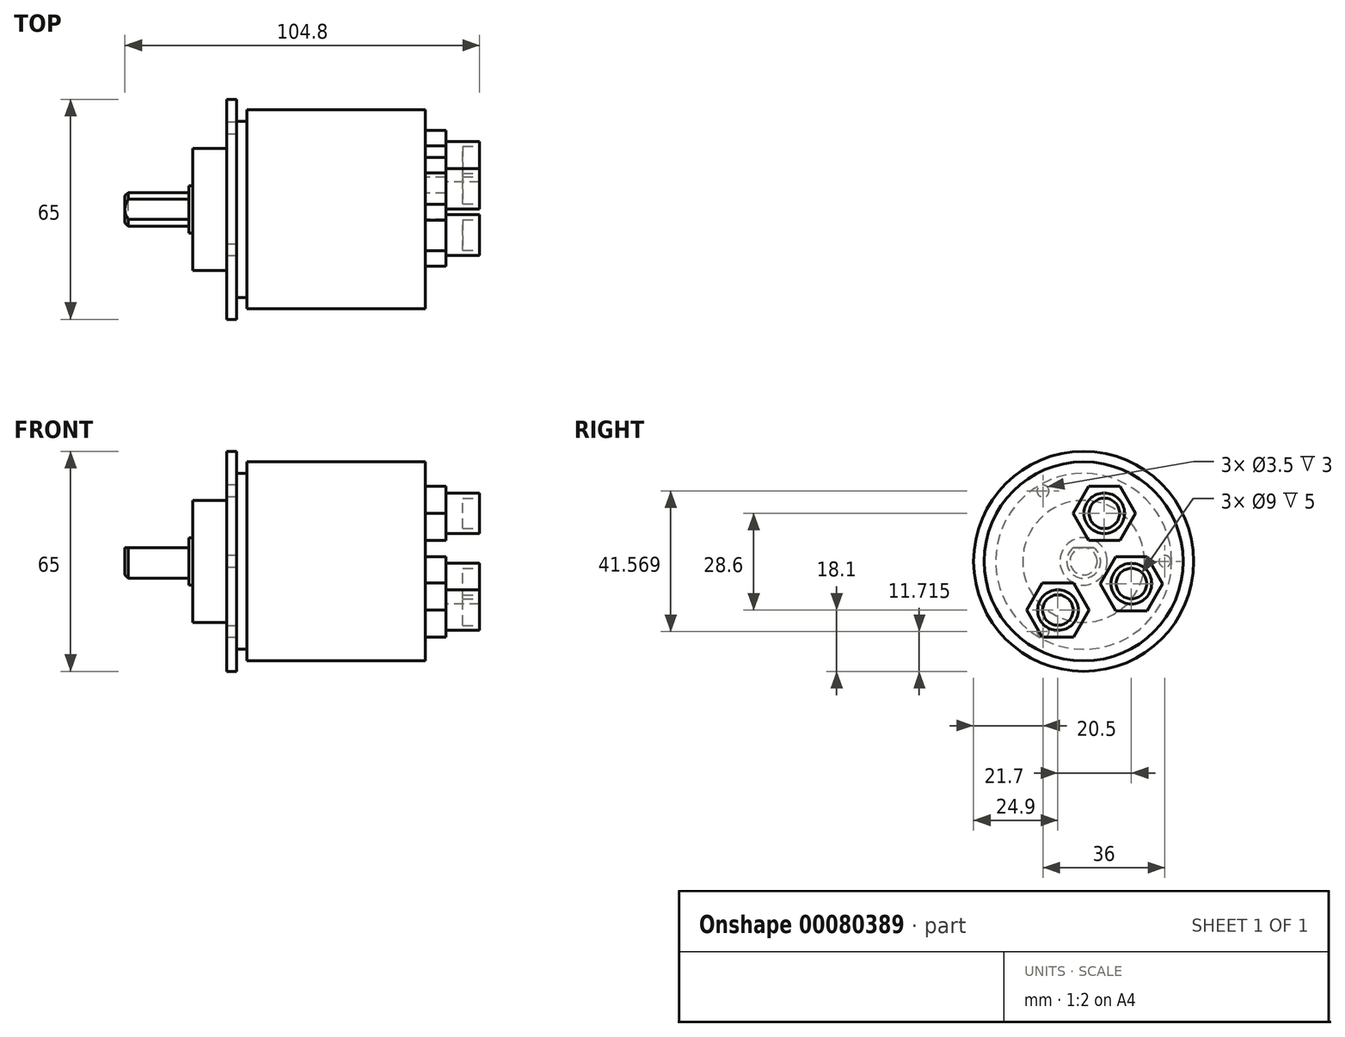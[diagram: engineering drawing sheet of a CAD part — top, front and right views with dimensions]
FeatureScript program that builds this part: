
annotation { "Feature Type Name" : "Feature", "Feature Type Description" : "" }
export const myFeature = defineFeature(function(context is Context, id is Id, definition is map)
    precondition{}
    {
        {
            var Q0;
            Q0=qCreatedBy(makeId("Right.planeOp"),FACE);
            var sketch = newSketch(context, id + "F0", { "sketchPlane" : qUnion([Q0])});
            skCircle(sketch, "E0", {"center": v(0, 0) * mm, "radius": 5 * mm});
            skSolve(sketch);
        }
        {
            var Q0;
            Q0=qSketchRegion(id+"F0",true);
            extrude(context, id + "F1", {"entities" : qUnion([Q0]), "oppositeDirection" : true, "depth" : 18.9 * mm});
        }
        {
            var Q0;
            Q0=qCreatedBy(makeId("Right.planeOp"),FACE);
            var sketch = newSketch(context, id + "F2", { "sketchPlane" : qUnion([Q0])});
            skLineSegment(sketch, "E1", {"start": v(-18, 0) * mm, "end": v(18.18, 0) * mm, "construction": true});
            skLineSegment(sketch, "E2.0", {"start": v(-18, 4) * mm, "end": v(18.18, 4) * mm});
            skLineSegment(sketch, "E3.bottom", {"start": v(-10.5, 4) * mm, "end": v(10.66, 4) * mm});
            skLineSegment(sketch, "E3.top", {"start": v(-10.5, 8.93) * mm, "end": v(10.66, 8.93) * mm});
            skLineSegment(sketch, "E3.left", {"start": v(-10.5, 4) * mm, "end": v(-10.5, 8.93) * mm});
            skLineSegment(sketch, "E3.right", {"start": v(10.66, 4) * mm, "end": v(10.66, 8.93) * mm});
            skLineSegment(sketch, "E4.0", {"start": v(-18, -5) * mm, "end": v(18.18, -5) * mm, "construction": true});
            skSolve(sketch);
        }
        {
            var Q0;
            Q0=qSketchRegion(id+"F2",true);
            extrude(context, id + "F3", {"entities" : qUnion([Q0]), "operationType" : NewBodyOperationType.REMOVE, "endBound" : BoundingType.THROUGH_ALL, "oppositeDirection" : true, "depth" : 25 * mm});
        }
        {
            var Q0;
            Q0=makeQuery(id+"F1.opExtrude","CAP_EDGE",EDGE,{"disambiguationData":[OSD([sQuery(id+"F0.wireOp",EDGE,"E0")])],"isStart":false});
            chamfer(context, id + "F4", {"entities" : qUnion([Q0]), "width" : 1 * mm, "tangentPropagation" : true});
        }
        {
            var Q0;
            Q0=makeQuery(id+"F1.opExtrude","CAP_FACE",FACE,{"disambiguationData":[OSD([sQuery(id+"F0.wireOp",EDGE,"E0")])],"isStart":true});
            var sketch = newSketch(context, id + "F5", { "sketchPlane" : qUnion([Q0])});
            skCircle(sketch, "E5", {"center": v(0, 0) * mm, "radius": 7 * mm});
            skSolve(sketch);
        }
        {
            var Q0;
            Q0=qSketchRegion(id+"F5",true);
            extrude(context, id + "F6", {"entities" : qUnion([Q0]), "operationType" : NewBodyOperationType.ADD, "depth" : 1.1 * mm});
        }
        {
            var Q0;
            Q0=makeQuery(id+"F6.opExtrude","CAP_FACE",FACE,{"disambiguationData":[OSD([sQuery(id+"F5.wireOp",EDGE,"E5")])],"isStart":false});
            var sketch = newSketch(context, id + "F7", { "sketchPlane" : qUnion([Q0])});
            skCircle(sketch, "E6", {"center": v(0, 0) * mm, "radius": 18 * mm});
            skSolve(sketch);
        }
        {
            var Q0;
            Q0=qSketchRegion(id+"F7",true);
            extrude(context, id + "F8", {"entities" : qUnion([Q0]), "operationType" : NewBodyOperationType.ADD, "depth" : 10 * mm});
        }
        {
            var Q0;
            Q0=makeQuery(id+"F8.opExtrude","CAP_FACE",FACE,{"disambiguationData":[OSD([sQuery(id+"F7.wireOp",EDGE,"E6")])],"isStart":false});
            var sketch = newSketch(context, id + "F9", { "sketchPlane" : qUnion([Q0])});
            skCircle(sketch, "E7", {"center": v(0, 0) * mm, "radius": 32.5 * mm});
            skSolve(sketch);
        }
        {
            var Q0;
            Q0=qSketchRegion(id+"F9",true);
            extrude(context, id + "F10", {"entities" : qUnion([Q0]), "operationType" : NewBodyOperationType.ADD, "depth" : 3 * mm});
        }
        {
            var Q0;
            Q0=makeQuery(id+"F10.opExtrude","CAP_FACE",FACE,{"disambiguationData":[OSD([sQuery(id+"F9.wireOp",EDGE,"E7")])],"isStart":false});
            var sketch = newSketch(context, id + "F11", { "sketchPlane" : qUnion([Q0])});
            skCircle(sketch, "E8", {"center": v(0, 0) * mm, "radius": 26 * mm});
            skSolve(sketch);
        }
        {
            var Q0;
            Q0=qSketchRegion(id+"F11",true);
            extrude(context, id + "F12", {"entities" : qUnion([Q0]), "operationType" : NewBodyOperationType.ADD, "depth" : 3 * mm});
        }
        {
            var Q0;
            Q0=makeQuery(id+"F10.opExtrude","CAP_FACE",FACE,{"disambiguationData":[OSD([sQuery(id+"F9.wireOp",EDGE,"E7")])],"isStart":true});
            cPlane(context, id + "F13", {"entities" : qUnion([Q0]), "cplaneType" : CPlaneType.OFFSET, "offset" : 58.8 * mm, "oppositeDirection" : true, "width" : 150 * mm, "height" : 150 * mm});
        }
        {
            var Q0;
            Q0=qCreatedBy(id+"F13.planeOp",FACE);
            var sketch = newSketch(context, id + "F14", { "sketchPlane" : qUnion([Q0])});
            skCircle(sketch, "E9", {"center": v(0, 0) * mm, "radius": 29.4 * mm});
            skSolve(sketch);
        }
        {
            var Q0;
            Q0=qSketchRegion(id+"F14",true);
            var Q1;
            Q1=makeQuery(id+"F12.opExtrude","CAP_FACE",FACE,{"disambiguationData":[OSD([sQuery(id+"F11.wireOp",EDGE,"E8")])],"isStart":false});
            extrude(context, id + "F15", {"entities" : qUnion([Q0]), "operationType" : NewBodyOperationType.ADD, "endBound" : BoundingType.UP_TO_SURFACE, "endBoundEntityFace" : qUnion([Q1]), "depth" : 25 * mm});
        }
        {
            var Q0;
            Q0=makeQuery(id+"F10.opExtrude","CAP_FACE",FACE,{"disambiguationData":[OSD([sQuery(id+"F9.wireOp",EDGE,"E7")])],"isStart":true});
            var sketch = newSketch(context, id + "F16", { "sketchPlane" : qUnion([Q0])});
            skLineSegment(sketch, "E10", {"start": v(0, 0) * mm, "end": v(-37.53, 0) * mm, "construction": true});
            skCircle(sketch, "E11", {"center": v(0, 0) * mm, "radius": 24 * mm, "construction": true});
            skPoint(sketch, "E12", {"position": v(-24, 0) * mm});
            skPoint(sketch, "E13.1.0", {"position": v(12, -20.78) * mm});
            skPoint(sketch, "E13.2.0", {"position": v(12, 20.78) * mm});
            skCircle(sketch, "E14", {"center": v(-24, 0) * mm, "radius": 1.75 * mm});
            skCircle(sketch, "E15.1.0", {"center": v(12, -20.78) * mm, "radius": 1.75 * mm});
            skCircle(sketch, "E15.2.0", {"center": v(12, 20.78) * mm, "radius": 1.75 * mm});
            skSolve(sketch);
        }
        {
            var Q0;
            Q0=qSketchRegion(id+"F16",true);
            extrude(context, id + "F17", {"entities" : qUnion([Q0]), "operationType" : NewBodyOperationType.REMOVE, "oppositeDirection" : true, "depth" : 3 * mm});
        }
        {
            var Q0;
            Q0=makeQuery(id+"F15.opExtrude","CAP_FACE",FACE,{"disambiguationData":[OSD([sQuery(id+"F14.wireOp",EDGE,"E9")])],"isStart":true});
            var sketch = newSketch(context, id + "F18", { "sketchPlane" : qUnion([Q0])});
            skLineSegment(sketch, "E16", {"start": v(0, 47.06) * mm, "end": v(0, -42.51) * mm, "construction": true});
            skLineSegment(sketch, "E17", {"start": v(0, 0) * mm, "end": v(46.06, 0) * mm, "construction": true});
            skLineSegment(sketch, "E18", {"start": v(0, 0) * mm, "end": v(42.94, -20.02) * mm, "construction": true});
            skLineSegment(sketch, "E19.0", {"start": v(14.1, 45.36) * mm, "end": v(14.1, -42.51) * mm, "construction": true});
            skLineSegment(sketch, "E20", {"start": v(0, 0) * mm, "end": v(-39.96, 0) * mm, "construction": true});
            skLineSegment(sketch, "E21.0", {"start": v(6.1, 14.2) * mm, "end": v(-39.96, 14.2) * mm, "construction": true});
            skLineSegment(sketch, "E22.0", {"start": v(6.1, 47.06) * mm, "end": v(6.1, -42.51) * mm, "construction": true});
            skPoint(sketch, "E23", {"position": v(6.1, 14.2) * mm});
            skPoint(sketch, "E24", {"position": v(14.1, -6.57) * mm});
            skLineSegment(sketch, "E25.0", {"start": v(0, -14.4) * mm, "end": v(-39.96, -14.4) * mm, "construction": true});
            skLineSegment(sketch, "E26.0", {"start": v(-7.6, 47.06) * mm, "end": v(-7.6, -42.51) * mm, "construction": true});
            skPoint(sketch, "E27", {"position": v(-7.6, -14.4) * mm});
            skCircle(sketch, "E28.cCircle", {"center": v(14.1, -6.57) * mm, "radius": 8 * mm});
            skLineSegment(sketch, "E28.0", {"start": v(9.48, 1.43) * mm, "end": v(18.72, 1.43) * mm});
            skLineSegment(sketch, "E28.1", {"start": v(18.72, 1.43) * mm, "end": v(23.34, -6.57) * mm});
            skLineSegment(sketch, "E28.2", {"start": v(23.34, -6.57) * mm, "end": v(18.72, -14.57) * mm});
            skLineSegment(sketch, "E28.3", {"start": v(18.72, -14.57) * mm, "end": v(9.48, -14.57) * mm});
            skLineSegment(sketch, "E28.4", {"start": v(9.48, -14.57) * mm, "end": v(4.86, -6.57) * mm});
            skLineSegment(sketch, "E28.5", {"start": v(4.86, -6.57) * mm, "end": v(9.48, 1.43) * mm});
            skPoint(sketch, "E28.0.midPoint", {"position": v(14.1, 1.43) * mm});
            skCircle(sketch, "E29.cCircle", {"center": v(6.1, 14.2) * mm, "radius": 8 * mm, "construction": true});
            skLineSegment(sketch, "E29.0", {"start": v(1.48, 22.2) * mm, "end": v(10.72, 22.2) * mm});
            skLineSegment(sketch, "E29.1", {"start": v(10.72, 22.2) * mm, "end": v(15.34, 14.2) * mm});
            skLineSegment(sketch, "E29.2", {"start": v(15.34, 14.2) * mm, "end": v(10.72, 6.2) * mm});
            skLineSegment(sketch, "E29.3", {"start": v(10.72, 6.2) * mm, "end": v(1.48, 6.2) * mm});
            skLineSegment(sketch, "E29.4", {"start": v(1.48, 6.2) * mm, "end": v(-3.14, 14.2) * mm});
            skLineSegment(sketch, "E29.5", {"start": v(-3.14, 14.2) * mm, "end": v(1.48, 22.2) * mm});
            skPoint(sketch, "E29.0.midPoint", {"position": v(6.1, 22.2) * mm});
            skCircle(sketch, "E30.cCircle", {"center": v(-7.6, -14.4) * mm, "radius": 8 * mm, "construction": true});
            skLineSegment(sketch, "E30.0", {"start": v(-12.22, -6.4) * mm, "end": v(-2.98, -6.4) * mm});
            skLineSegment(sketch, "E30.1", {"start": v(-2.98, -6.4) * mm, "end": v(1.64, -14.4) * mm});
            skLineSegment(sketch, "E30.2", {"start": v(1.64, -14.4) * mm, "end": v(-2.98, -22.4) * mm});
            skLineSegment(sketch, "E30.3", {"start": v(-2.98, -22.4) * mm, "end": v(-12.22, -22.4) * mm});
            skLineSegment(sketch, "E30.4", {"start": v(-12.22, -22.4) * mm, "end": v(-16.84, -14.4) * mm});
            skLineSegment(sketch, "E30.5", {"start": v(-16.84, -14.4) * mm, "end": v(-12.22, -6.4) * mm});
            skPoint(sketch, "E30.0.midPoint", {"position": v(-7.6, -6.4) * mm});
            skSolve(sketch);
        }
        {
            var Q0;
            Q0=qSketchRegion(id+"F18",true);
            extrude(context, id + "F19", {"entities" : qUnion([Q0]), "operationType" : NewBodyOperationType.ADD, "depth" : 6 * mm});
        }
        {
            var Q0;
            Q0=makeQuery(id+"F19.opExtrude","CAP_FACE",FACE,{"disambiguationData":[OSD([sQuery(id+"F18.wireOp",EDGE,"E29.0"),sQuery(id+"F18.wireOp",EDGE,"E29.1"),sQuery(id+"F18.wireOp",EDGE,"E29.2"),sQuery(id+"F18.wireOp",EDGE,"E29.3"),sQuery(id+"F18.wireOp",EDGE,"E29.4"),sQuery(id+"F18.wireOp",EDGE,"E29.5")])],"isStart":false});
            var sketch = newSketch(context, id + "F20", { "sketchPlane" : qUnion([Q0])});
            skPoint(sketch, "E31.0", {"position": v(6.1, 14.2) * mm});
            skPoint(sketch, "E32.0", {"position": v(14.1, -6.57) * mm});
            skPoint(sketch, "E33.0", {"position": v(-7.6, -14.4) * mm});
            skCircle(sketch, "E34", {"center": v(6.1, 14.2) * mm, "radius": 6 * mm});
            skCircle(sketch, "E35", {"center": v(14.1, -6.57) * mm, "radius": 6 * mm});
            skCircle(sketch, "E36", {"center": v(-7.6, -14.4) * mm, "radius": 6 * mm});
            skSolve(sketch);
        }
        {
            var Q0;
            Q0=qSketchRegion(id+"F20",true);
            extrude(context, id + "F21", {"entities" : qUnion([Q0]), "operationType" : NewBodyOperationType.ADD, "depth" : 10 * mm});
        }
        {
            var Q0;
            Q0=makeQuery(id+"F21.opExtrude","CAP_FACE",FACE,{"disambiguationData":[OSD([sQuery(id+"F20.wireOp",EDGE,"E34")])],"isStart":false});
            var sketch = newSketch(context, id + "F22", { "sketchPlane" : qUnion([Q0])});
            skCircle(sketch, "E37.0", {"center": v(6.1, 14.2) * mm, "radius": 6 * mm, "construction": true});
            skCircle(sketch, "E38.0", {"center": v(14.1, -6.57) * mm, "radius": 6 * mm, "construction": true});
            skCircle(sketch, "E39.0", {"center": v(-7.6, -14.4) * mm, "radius": 6 * mm, "construction": true});
            skCircle(sketch, "E40.0", {"center": v(6.1, 14.2) * mm, "radius": 4.5 * mm});
            skCircle(sketch, "E41", {"center": v(-7.6, -14.4) * mm, "radius": 4.5 * mm});
            skCircle(sketch, "E42", {"center": v(14.1, -6.57) * mm, "radius": 4.5 * mm});
            skSolve(sketch);
        }
        {
            var Q0;
            Q0=qSketchRegion(id+"F22",true);
            extrude(context, id + "F23", {"entities" : qUnion([Q0]), "operationType" : NewBodyOperationType.REMOVE, "oppositeDirection" : true, "depth" : 5 * mm});
        }
    });
